# Revit family: HOSPITAIR G - MVX 4-5 - MVA 9 - MVB 12-16 - MVC 19-23
name_source: partatom
category: Equipement spécialisé
revit_build: Autodesk Revit 2018 (Build: 20170223_1515(x64)
units: mm (PartAtom-declared; Revit-internal decimal feet)

## family parameters
Basée sur le plan de construction = Non
Cote de connecteur circulaire = Utiliser le diamètre
Couper avec des vides une fois chargée = Non
Partagée = Non
Point de calcul de pièce = Non
Toujours verticalement = Oui
Type d'élément = Normal

## types (7) — shared parameters
COS_PHI = 0.9
DOUBLE_ALIMENTATION = Non
Decalage_Bouton_Bord = 110 mm  [stored 0.360892 ft]
Decalage_Ecran_Bord = 100 mm  [stored 0.328084 ft]
Decalage_Pieds_Compresseur = 60 mm  [stored 0.19685 ft]
Epaisseur_Ecran = 20 mm  [stored 0.0656168 ft]
Epaisseur_Gaine_Rejet = 22 mm  [stored 0.0721785 ft]
FREQUENCE = 50 Hz
Fabricant = MIL'S
Hauteur_Ecran = 180 mm  [stored 0.590551 ft]
Hauteur_Pieds = 100 mm  [stored 0.328084 ft]
Largeur_Ecran = 150 mm
Lien espace client = https://www.mils.fr
Longueur_Ecran = 190 mm
NBR_POLES = 3
NEUTRE = Non
Rayon_Pieds = 50 mm  [stored 0.164042 ft]
TENSION_ALIM = 400 V
TERRE = Oui
Zone_Maintenance_Arrière = 200 mm  [stored 0.656168 ft]
zero-valued in all types: DIAM_ASPI_AIR, Zone_Maintenance_Hauteur

## per-type parameters (varying)
- MVX 4: DESCR_ALIM_X=Alimentation X ; 4G2.5mm²; DESCR_ASPI=Aspiration Air ; 1028.8m3/h; DESCR_REFOUL=Refoulement Air ; 28.8 m3/h ; G 3/4" MAL; DESCR_VENTIL_AIR=Ventilation Air ; 1000 m3/h ;; DIAM_REFOUL_AIR=20 mm  [stored 0.0656168 ft]; Debit_aspiration_air=1028.8 m³/h; Debit_refoulement_air=28.8 m³/h; Debit_ventilation_air=1000.0 m³/h; Decalage_Gaine_Bloc=205 mm; Decalage_Horizontal_Grille_Gaine_Rejet=22 mm  [stored 0.0721785 ft]; Decalage_Vertical_Grille_Gaine_Rejet=22 mm  [stored 0.0721785 ft]; Decalage_horizontal_connecteur_elec=515 mm; Decalage_horizontal_connecteur_sortie_Air=43 mm  [stored 0.141076 ft]; Decalage_vertical_connecteur_elec=174 mm  [stored 0.570866 ft]; Decalage_vertical_connecteur_sortie_Air=522 mm; Diametre_Plaque_Connecteur_Elec=33 mm  [stored 0.108268 ft]; Entraxe_Pieds_1=470 mm; Entraxe_Pieds_2=430 mm; Epaisseur_Plaque_Gaine=890 mm; Epaisseur_Porte=40 mm  [stored 0.131234 ft]; HAUTEUR=970 mm; Hauteur_Bas_Ecran=790 mm; Hauteur_Bloc_Gaine=900 mm; Hauteur_Bouton=850 mm; Hauteur_Gaine_Rejet=108 mm  [stored 0.354331 ft]; Hauteur_Globale_Compresseur=970 mm; Hauteur_Hors_Ecran=950 mm; LARGEUR=590 mm; LONGUEUR=632 mm; Largeur_Gaine_Rejet=504 mm; Largeur_Globale_Compresseur=590 mm; Largeur_Porte=385 mm; Modèle=HOSPITAIR G - 11 bar - MVX 4; NIVEAU_SONORE(dB(A))=62; POIDS(Kg)=145 mm  [stored 0.475722 ft]; PROTEC_ELECT_X=Disjoncteur coube D - 16 A; PUISS_APPARENTE_X=4444 VA; PUISS_ELECT_X=4 kW; Profondeur_Globale_Compresseur=632 mm; Rayon_Plaque_Connecteur_Elec=17 mm; Rayon_Plaque_Connecteur_Sortie_Air=10 mm  [stored 0.0328084 ft]; ZONE_MAINTENANCE=Non; Zone_Maintenance_Avant=800 mm; Zone_Maintenance_Droite=800 mm; Zone_Maintenance_Gauche=800 mm
- MVX 5: DESCR_ALIM_X=Alimentation X ; 4G2.5mm²; DESCR_ASPI=Aspiration Air ; 1340.2m3/h; DESCR_REFOUL=Refoulement Air ; 40.2 m3/h ; G 3/4" MAL; DESCR_VENTIL_AIR=Ventilation Air ; 1300 m3/h ;; DIAM_REFOUL_AIR=20 mm  [stored 0.0656168 ft]; Debit_aspiration_air=1340.2 m³/h; Debit_refoulement_air=40.2 m³/h; Debit_ventilation_air=1300.0 m³/h; Decalage_Gaine_Bloc=205 mm; Decalage_Horizontal_Grille_Gaine_Rejet=22 mm  [stored 0.0721785 ft]; Decalage_Vertical_Grille_Gaine_Rejet=22 mm  [stored 0.0721785 ft]; Decalage_horizontal_connecteur_elec=515 mm; Decalage_horizontal_connecteur_sortie_Air=43 mm  [stored 0.141076 ft]; Decalage_vertical_connecteur_elec=174 mm  [stored 0.570866 ft]; Decalage_vertical_connecteur_sortie_Air=522 mm; Diametre_Plaque_Connecteur_Elec=33 mm  [stored 0.108268 ft]; Entraxe_Pieds_1=470 mm; Entraxe_Pieds_2=430 mm; Epaisseur_Plaque_Gaine=890 mm; Epaisseur_Porte=40 mm  [stored 0.131234 ft]; HAUTEUR=970 mm; Hauteur_Bas_Ecran=790 mm; Hauteur_Bloc_Gaine=900 mm; Hauteur_Bouton=850 mm; Hauteur_Gaine_Rejet=108 mm  [stored 0.354331 ft]; Hauteur_Globale_Compresseur=970 mm; Hauteur_Hors_Ecran=950 mm; LARGEUR=590 mm; LONGUEUR=632 mm; Largeur_Gaine_Rejet=504 mm; Largeur_Globale_Compresseur=590 mm; Largeur_Porte=385 mm; Modèle=HOSPITAIR G - 11 bar - MVX 5; NIVEAU_SONORE(dB(A))=64; POIDS(Kg)=155 mm  [stored 0.50853 ft]; PROTEC_ELECT_X=Disjoncteur coube D - 16 A; PUISS_APPARENTE_X=6111 VA; PUISS_ELECT_X=6 kW; Profondeur_Globale_Compresseur=632 mm; Rayon_Plaque_Connecteur_Elec=17 mm; Rayon_Plaque_Connecteur_Sortie_Air=10 mm  [stored 0.0328084 ft]; ZONE_MAINTENANCE=Non; Zone_Maintenance_Avant=800 mm; Zone_Maintenance_Droite=800 mm; Zone_Maintenance_Gauche=800 mm
- MVA 9: DESCR_ALIM_X=Alimentation X ; 4G2.5mm²; DESCR_ASPI=Aspiration Air ; 2165m3/h; DESCR_REFOUL=Refoulement Air ; 65 m3/h ; G 3/4" MAL; DESCR_VENTIL_AIR=Ventilation Air ; 2100 m3/h ;; DIAM_REFOUL_AIR=20 mm  [stored 0.0656168 ft]; Debit_aspiration_air=2165.0 m³/h; Debit_refoulement_air=65.0 m³/h; Debit_ventilation_air=2100.0 m³/h; Decalage_Gaine_Bloc=200 mm  [stored 0.656168 ft]; Decalage_Horizontal_Grille_Gaine_Rejet=22 mm  [stored 0.0721785 ft]; Decalage_Vertical_Grille_Gaine_Rejet=20 mm  [stored 0.0656168 ft]; Decalage_horizontal_connecteur_elec=647 mm; Decalage_horizontal_connecteur_sortie_Air=47 mm  [stored 0.154199 ft]; Decalage_vertical_connecteur_elec=190 mm; Decalage_vertical_connecteur_sortie_Air=578 mm; Diametre_Plaque_Connecteur_Elec=41 mm  [stored 0.134514 ft]; Entraxe_Pieds_1=510 mm; Entraxe_Pieds_2=578 mm; Epaisseur_Plaque_Gaine=1020 mm; Epaisseur_Porte=50 mm  [stored 0.164042 ft]; HAUTEUR=1100 mm; Hauteur_Bas_Ecran=920 mm; Hauteur_Bloc_Gaine=1030 mm; Hauteur_Bouton=950 mm; Hauteur_Gaine_Rejet=130 mm  [stored 0.426509 ft]; Hauteur_Globale_Compresseur=1100 mm; Hauteur_Hors_Ecran=1080 mm; LARGEUR=630 mm; LONGUEUR=790 mm; Largeur_Gaine_Rejet=658 mm; Largeur_Globale_Compresseur=630 mm; Largeur_Porte=430 mm; Modèle=HOSPITAIR G - 11 bar - MVA 9; NIVEAU_SONORE(dB(A))=65; POIDS(Kg)=240 mm  [stored 0.787402 ft]; PROTEC_ELECT_X=Disjoncteur coube D - 25 A; PUISS_APPARENTE_X=8333 VA; PUISS_ELECT_X=8 kW; Profondeur_Globale_Compresseur=790 mm; Rayon_Plaque_Connecteur_Elec=21 mm; Rayon_Plaque_Connecteur_Sortie_Air=10 mm  [stored 0.0328084 ft]; ZONE_MAINTENANCE=Oui; Zone_Maintenance_Avant=1000 mm; Zone_Maintenance_Droite=1000 mm; Zone_Maintenance_Gauche=1000 mm
- MVB 12: DESCR_ALIM_X=Alimentation X ; 4G6mm²; DESCR_ASPI=Aspiration Air ; 2601m3/h; DESCR_REFOUL=Refoulement Air ; 101 m3/h ; G 1" MAL; DESCR_VENTIL_AIR=Ventilation Air ; 2500 m3/h ; 768 x 152 mm ;; DIAM_REFOUL_AIR=25 mm  [stored 0.082021 ft]; Debit_aspiration_air=2601.0 m³/h; Debit_refoulement_air=101.0 m³/h; Debit_ventilation_air=2500.0 m³/h; Decalage_Gaine_Bloc=176 mm; Decalage_Horizontal_Grille_Gaine_Rejet=22 mm  [stored 0.0721785 ft]; Decalage_Vertical_Grille_Gaine_Rejet=25 mm  [stored 0.082021 ft]; Decalage_horizontal_connecteur_elec=689 mm; Decalage_horizontal_connecteur_sortie_Air=47 mm  [stored 0.154199 ft]; Decalage_vertical_connecteur_elec=177 mm  [stored 0.580709 ft]; Decalage_vertical_connecteur_sortie_Air=605 mm; Diametre_Plaque_Connecteur_Elec=41 mm  [stored 0.134514 ft]; Entraxe_Pieds_1=630 mm; Entraxe_Pieds_2=685 mm; Epaisseur_Plaque_Gaine=1180 mm; Epaisseur_Porte=48 mm  [stored 0.15748 ft]; HAUTEUR=1260 mm; Hauteur_Bas_Ecran=1080 mm; Hauteur_Bloc_Gaine=1190 mm; Hauteur_Bouton=1110 mm; Hauteur_Gaine_Rejet=152 mm  [stored 0.498688 ft]; Hauteur_Globale_Compresseur=1260 mm; Hauteur_Hors_Ecran=1240 mm; LARGEUR=750 mm; LONGUEUR=895 mm; Largeur_Gaine_Rejet=768 mm; Largeur_Globale_Compresseur=750 mm; Largeur_Porte=574 mm; Modèle=HOSPITAIR G - 11 bar - MVB 12; NIVEAU_SONORE(dB(A))=66; POIDS(Kg)=312 mm; PROTEC_ELECT_X=Disjoncteur coube D - 32 A; PUISS_APPARENTE_X=12222 VA; PUISS_ELECT_X=11 kW; Profondeur_Globale_Compresseur=895 mm; Rayon_Plaque_Connecteur_Elec=21 mm; Rayon_Plaque_Connecteur_Sortie_Air=13 mm; ZONE_MAINTENANCE=Oui; Zone_Maintenance_Avant=1000 mm; Zone_Maintenance_Droite=1000 mm; Zone_Maintenance_Gauche=1000 mm
- MVB 16: DESCR_ALIM_X=Alimentation X ; 4G6mm²; DESCR_ASPI=Aspiration Air ; 3127m3/h; DESCR_REFOUL=Refoulement Air ; 127 m3/h ; G 1" MAL; DESCR_VENTIL_AIR=Ventilation Air ; 3000 m3/h ; 768 x 152 mm ;; DIAM_REFOUL_AIR=25 mm  [stored 0.082021 ft]; Debit_aspiration_air=3127.0 m³/h; Debit_refoulement_air=127.0 m³/h; Debit_ventilation_air=3000.0 m³/h; Decalage_Gaine_Bloc=176 mm; Decalage_Horizontal_Grille_Gaine_Rejet=22 mm  [stored 0.0721785 ft]; Decalage_Vertical_Grille_Gaine_Rejet=25 mm  [stored 0.082021 ft]; Decalage_horizontal_connecteur_elec=689 mm; Decalage_horizontal_connecteur_sortie_Air=47 mm  [stored 0.154199 ft]; Decalage_vertical_connecteur_elec=177 mm  [stored 0.580709 ft]; Decalage_vertical_connecteur_sortie_Air=605 mm; Diametre_Plaque_Connecteur_Elec=41 mm  [stored 0.134514 ft]; Entraxe_Pieds_1=630 mm; Entraxe_Pieds_2=685 mm; Epaisseur_Plaque_Gaine=1180 mm; Epaisseur_Porte=48 mm  [stored 0.15748 ft]; HAUTEUR=1260 mm; Hauteur_Bas_Ecran=1080 mm; Hauteur_Bloc_Gaine=1190 mm; Hauteur_Bouton=1110 mm; Hauteur_Gaine_Rejet=152 mm  [stored 0.498688 ft]; Hauteur_Globale_Compresseur=1260 mm; Hauteur_Hors_Ecran=1240 mm; LARGEUR=750 mm; LONGUEUR=895 mm; Largeur_Gaine_Rejet=768 mm; Largeur_Globale_Compresseur=750 mm; Largeur_Porte=574 mm; Modèle=HOSPITAIR G - 11 bar - MVB 16; NIVEAU_SONORE(dB(A))=67; POIDS(Kg)=320 mm; PROTEC_ELECT_X=Disjoncteur coube D - 40 A; PUISS_APPARENTE_X=16667 VA; PUISS_ELECT_X=15 kW; Profondeur_Globale_Compresseur=895 mm; Rayon_Plaque_Connecteur_Elec=21 mm; Rayon_Plaque_Connecteur_Sortie_Air=13 mm; ZONE_MAINTENANCE=Non; Zone_Maintenance_Avant=1000 mm; Zone_Maintenance_Droite=1000 mm; Zone_Maintenance_Gauche=1000 mm
- MVC 19: DESCR_ALIM_X=Alimentation X ; 4G10mm²; DESCR_ASPI=Aspiration Air ; 4179m3/h; DESCR_REFOUL=Refoulement Air ; 179 m3/h ; G 1"1/4 MAL; DESCR_VENTIL_AIR=Ventilation Air ; 4000 m3/h ; 870 x 680 mm ;; DIAM_REFOUL_AIR=32 mm  [stored 0.104987 ft]; Debit_aspiration_air=4179.0 m³/h; Debit_refoulement_air=179.0 m³/h; Debit_ventilation_air=4000.0 m³/h; Decalage_Gaine_Bloc=230 mm; Decalage_Horizontal_Grille_Gaine_Rejet=326 mm; Decalage_Vertical_Grille_Gaine_Rejet=32 mm  [stored 0.104987 ft]; Decalage_horizontal_connecteur_elec=742 mm; Decalage_horizontal_connecteur_sortie_Air=56 mm  [stored 0.183727 ft]; Decalage_vertical_connecteur_elec=193 mm  [stored 0.633202 ft]; Decalage_vertical_connecteur_sortie_Air=850 mm; Diametre_Plaque_Connecteur_Elec=58 mm  [stored 0.190289 ft]; Entraxe_Pieds_1=680 mm; Entraxe_Pieds_2=870 mm; Epaisseur_Plaque_Gaine=1450 mm; Epaisseur_Porte=58 mm  [stored 0.190289 ft]; HAUTEUR=1530 mm; Hauteur_Bas_Ecran=1350 mm; Hauteur_Bloc_Gaine=1460 mm; Hauteur_Bouton=1380 mm; Hauteur_Gaine_Rejet=262 mm  [stored 0.85958 ft]; Hauteur_Globale_Compresseur=1530 mm; Hauteur_Hors_Ecran=1510 mm; LARGEUR=800 mm; LONGUEUR=1110 mm; Largeur_Gaine_Rejet=646 mm; Largeur_Globale_Compresseur=800 mm; Largeur_Porte=570 mm; Modèle=HOSPITAIR G - 11 bar - MVC 19; NIVEAU_SONORE(dB(A))=69; POIDS(Kg)=505 mm; PROTEC_ELECT_X=Disjoncteur coube D - 63 A; PUISS_APPARENTE_X=20556 VA; PUISS_ELECT_X=19 kW; Profondeur_Globale_Compresseur=1110 mm; Rayon_Plaque_Connecteur_Elec=29 mm  [stored 0.0951444 ft]; Rayon_Plaque_Connecteur_Sortie_Air=16 mm  [stored 0.0524934 ft]; ZONE_MAINTENANCE=Non; Zone_Maintenance_Avant=1000 mm; Zone_Maintenance_Droite=1000 mm; Zone_Maintenance_Gauche=1000 mm
- MVC 23: DESCR_ALIM_X=Alimentation X ; 4G10mm²; DESCR_ASPI=Aspiration Air ; 5210 m3/h; DESCR_REFOUL=Refoulement Air ; 210 m3/h ; G 1"1/4 MAL; DESCR_VENTIL_AIR=Ventilation Air ; 5000 m3/h ; 646 x 262 mm ;; DIAM_REFOUL_AIR=32 mm  [stored 0.104987 ft]; Debit_aspiration_air=5210.0 m³/h; Debit_refoulement_air=210.0 m³/h; Debit_ventilation_air=5000.0 m³/h; Decalage_Gaine_Bloc=230 mm; Decalage_Horizontal_Grille_Gaine_Rejet=326 mm; Decalage_Vertical_Grille_Gaine_Rejet=32 mm  [stored 0.104987 ft]; Decalage_horizontal_connecteur_elec=742 mm; Decalage_horizontal_connecteur_sortie_Air=56 mm  [stored 0.183727 ft]; Decalage_vertical_connecteur_elec=193 mm  [stored 0.633202 ft]; Decalage_vertical_connecteur_sortie_Air=850 mm; Diametre_Plaque_Connecteur_Elec=58 mm  [stored 0.190289 ft]; Entraxe_Pieds_1=680 mm; Entraxe_Pieds_2=870 mm; Epaisseur_Plaque_Gaine=1450 mm; Epaisseur_Porte=58 mm  [stored 0.190289 ft]; HAUTEUR=1530 mm; Hauteur_Bas_Ecran=1350 mm; Hauteur_Bloc_Gaine=1460 mm; Hauteur_Bouton=1380 mm; Hauteur_Gaine_Rejet=262 mm  [stored 0.85958 ft]; Hauteur_Globale_Compresseur=1530 mm; Hauteur_Hors_Ecran=1510 mm; LARGEUR=800 mm; LONGUEUR=1110 mm; Largeur_Gaine_Rejet=646 mm; Largeur_Globale_Compresseur=800 mm; Largeur_Porte=570 mm; Modèle=HOSPITAIR G - 11 bar - MVC 23; NIVEAU_SONORE(dB(A))=71; POIDS(Kg)=525 mm; PROTEC_ELECT_X=Disjoncteur coube D - 63 A; PUISS_APPARENTE_X=24444 VA; PUISS_ELECT_X=22 kW; Profondeur_Globale_Compresseur=1110 mm; Rayon_Plaque_Connecteur_Elec=29 mm  [stored 0.0951444 ft]; Rayon_Plaque_Connecteur_Sortie_Air=16 mm  [stored 0.0524934 ft]; ZONE_MAINTENANCE=Non; Zone_Maintenance_Avant=1000 mm; Zone_Maintenance_Droite=1000 mm; Zone_Maintenance_Gauche=1000 mm

note: [stored X ft] marks values corroborated as IEEE doubles in the binary element streams (Revit-internal decimal feet)
